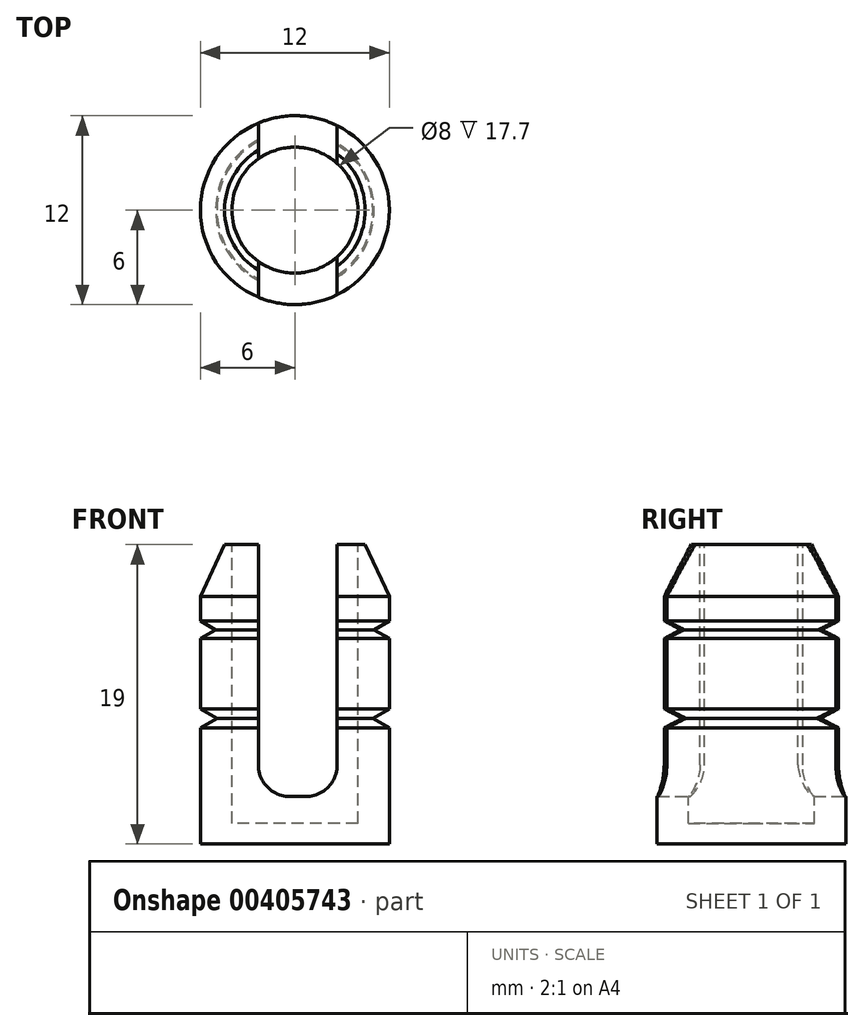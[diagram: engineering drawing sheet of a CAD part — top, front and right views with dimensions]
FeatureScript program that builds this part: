
annotation { "Feature Type Name" : "Feature", "Feature Type Description" : "" }
export const myFeature = defineFeature(function(context is Context, id is Id, definition is map)
    precondition{}
    {
        {
            var Q0;
            Q0=qCreatedBy(makeId("Top.planeOp"),FACE);
            var sketch = newSketch(context, id + "F0", { "sketchPlane" : qUnion([Q0])});
            skCircle(sketch, "E0", {"center": v(0, 0) * mm, "radius": 6 * mm});
            skSolve(sketch);
        }
        {
            var Q0;
            Q0=makeQuery(id+"F0.imprint","IMPRINT",FACE,{"disambiguationData":[TD([[makeQuery(id+"F0.imprint","IMPRINT",EDGE,{"derivedFrom":sQuery(id+"F0.wireOp",EDGE,"E0")}),1.0]])]});
            extrude(context, id + "F1", {"entities" : qUnion([Q0]), "depth" : 20 * mm});
        }
        {
            var Q0;
            Q0=makeQuery(id+"F1.opExtrude","CAP_FACE",FACE,{"disambiguationData":[OSD([sQuery(id+"F0.wireOp",EDGE,"E0")])],"isStart":false});
            var sketch = newSketch(context, id + "F2", { "sketchPlane" : qUnion([Q0])});
            skCircle(sketch, "E1", {"center": v(0, 0) * mm, "radius": 4 * mm});
            skSolve(sketch);
        }
        {
            var Q0;
            Q0 = qSketchRegion(id + "F2", true);
            extrude(context, id + "F3", {"entities" : qUnion([Q0]), "operationType" : NewBodyOperationType.REMOVE, "oppositeDirection" : true, "depth" : 18.7 * mm});
        }
        {
            var Q0;
            Q0=qCreatedBy(makeId("Front.planeOp"),FACE);
            var sketch = newSketch(context, id + "F4", { "sketchPlane" : qUnion([Q0])});
            skLineSegment(sketch, "E2", {"start": v(2.68, 16.25) * mm, "end": v(2.68, 3) * mm});
            skLineSegment(sketch, "E3", {"start": v(2.68, 3) * mm, "end": v(-2.32, 3) * mm});
            skLineSegment(sketch, "E4", {"start": v(-2.32, 3) * mm, "end": v(-2.32, 20) * mm});
            skLineSegment(sketch, "E5", {"start": v(-2.32, 20) * mm, "end": v(2.68, 20) * mm});
            skLineSegment(sketch, "E6", {"start": v(2.68, 20) * mm, "end": v(2.68, 16.25) * mm});
            skSolve(sketch);
        }
        {
            var Q0;
            Q0 = qSketchRegion(id + "F4", true);
            extrude(context, id + "F5", {"entities" : qUnion([Q0]), "operationType" : NewBodyOperationType.REMOVE, "endBound" : BoundingType.SYMMETRIC, "depth" : 25 * mm});
        }
        {
            var Q0;
            Q0=makeQuery(id+"F5.boolean.opBoolean","COPY",EDGE,{"disambiguationData":[OD(1.0)],"derivedFrom":makeQuery(id+"F5.opExtrude","SWEPT_EDGE",EDGE,{"disambiguationData":[OSD([sQuery(id+"F4.wireOp",EDGE,"E2"),sQuery(id+"F4.wireOp",EDGE,"E3")])]})});
            var Q1;
            Q1=makeQuery(id+"F5.boolean.opBoolean","COPY",EDGE,{"disambiguationData":[OD(1.0)],"derivedFrom":makeQuery(id+"F5.opExtrude","SWEPT_EDGE",EDGE,{"disambiguationData":[OSD([sQuery(id+"F4.wireOp",EDGE,"E3"),sQuery(id+"F4.wireOp",EDGE,"E4")])]})});
            var Q2;
            Q2=makeQuery(id+"F5.boolean.opBoolean","COPY",EDGE,{"disambiguationData":[OD(0.0)],"derivedFrom":makeQuery(id+"F5.opExtrude","SWEPT_EDGE",EDGE,{"disambiguationData":[OSD([sQuery(id+"F4.wireOp",EDGE,"E2"),sQuery(id+"F4.wireOp",EDGE,"E3")])]})});
            var Q3;
            Q3=makeQuery(id+"F5.boolean.opBoolean","COPY",EDGE,{"disambiguationData":[OD(0.0)],"derivedFrom":makeQuery(id+"F5.opExtrude","SWEPT_EDGE",EDGE,{"disambiguationData":[OSD([sQuery(id+"F4.wireOp",EDGE,"E3"),sQuery(id+"F4.wireOp",EDGE,"E4")])]})});
            fillet(context, id + "F6", {"entities" : qUnion([Q0, Q1, Q2, Q3]), "radius" : 2 * mm, "tangentPropagation" : true, "allowEdgeOverflow" : false});
        }
        {
            var Q0;
            {var subQ0=sQuery(id+"F0.wireOp",EDGE,"E0");Q0=makeQuery(id+"F5.boolean.opBoolean","SPLIT",EDGE,{"disambiguationData":[TD([makeQuery(id+"F5.opExtrude","SWEPT_FACE",FACE,{"disambiguationData":[OSD([sQuery(id+"F4.wireOp",EDGE,"E2"),sQuery(id+"F4.wireOp",EDGE,"E6")])]})])],"derivedFrom":makeQuery(id+"F1.opExtrude","CAP_EDGE",EDGE,{"disambiguationData":[OSD([subQ0])],"isStart":false})});}
            var Q1;
            {var subQ0=sQuery(id+"F0.wireOp",EDGE,"E0");Q1=makeQuery(id+"F5.boolean.opBoolean","SPLIT",EDGE,{"disambiguationData":[TD([makeQuery(id+"F5.opExtrude","SWEPT_FACE",FACE,{"disambiguationData":[OSD([sQuery(id+"F4.wireOp",EDGE,"E4")])]})])],"derivedFrom":makeQuery(id+"F1.opExtrude","CAP_EDGE",EDGE,{"disambiguationData":[OSD([subQ0])],"isStart":false})});}
            chamfer(context, id + "F7", {"entities" : qUnion([Q0, Q1]), "chamferType" : ChamferType.OFFSET_ANGLE, "width" : 2 * mm, "oppositeDirection" : false, "angle" : 65 * degree, "tangentPropagation" : true});
        }
        {
            var Q0;
            {var subQ0=sQuery(id+"F0.wireOp",EDGE,"E0");Q0=makeQuery(id+"F7.opChamfer","BLEND_EDGE",EDGE,{"blendedFrom":[makeQuery(id+"F5.boolean.opBoolean","SPLIT",EDGE,{"disambiguationData":[TD([makeQuery(id+"F5.opExtrude","SWEPT_FACE",FACE,{"disambiguationData":[OSD([sQuery(id+"F4.wireOp",EDGE,"E4")])]})])],"derivedFrom":makeQuery(id+"F1.opExtrude","CAP_EDGE",EDGE,{"disambiguationData":[OSD([subQ0])],"isStart":false})}),makeQuery(id+"F3.boolean.opBoolean","COPY",FACE,{"derivedFrom":makeQuery(id+"F3.opExtrude","SWEPT_FACE",FACE,{"disambiguationData":[OSD([sQuery(id+"F2.wireOp",EDGE,"E1")])]})})],"blendedInto":[makeQuery(id+"F3.boolean.opBoolean","COPY",FACE,{"derivedFrom":makeQuery(id+"F3.opExtrude","SWEPT_FACE",FACE,{"disambiguationData":[OSD([sQuery(id+"F2.wireOp",EDGE,"E1")])]})})]});}
            var Q1;
            {var subQ0=sQuery(id+"F0.wireOp",EDGE,"E0");Q1=makeQuery(id+"F7.opChamfer","BLEND_EDGE",EDGE,{"blendedFrom":[makeQuery(id+"F5.boolean.opBoolean","SPLIT",EDGE,{"disambiguationData":[TD([makeQuery(id+"F5.opExtrude","SWEPT_FACE",FACE,{"disambiguationData":[OSD([sQuery(id+"F4.wireOp",EDGE,"E2"),sQuery(id+"F4.wireOp",EDGE,"E6")])]})])],"derivedFrom":makeQuery(id+"F1.opExtrude","CAP_EDGE",EDGE,{"disambiguationData":[OSD([subQ0])],"isStart":false})}),makeQuery(id+"F3.boolean.opBoolean","COPY",FACE,{"derivedFrom":makeQuery(id+"F3.opExtrude","SWEPT_FACE",FACE,{"disambiguationData":[OSD([sQuery(id+"F2.wireOp",EDGE,"E1")])]})})],"blendedInto":[makeQuery(id+"F3.boolean.opBoolean","COPY",FACE,{"derivedFrom":makeQuery(id+"F3.opExtrude","SWEPT_FACE",FACE,{"disambiguationData":[OSD([sQuery(id+"F2.wireOp",EDGE,"E1")])]})})]});}
            chamfer(context, id + "F8", {"entities" : qUnion([Q0, Q1]), "chamferType" : ChamferType.OFFSET_ANGLE, "width" : 1 * mm, "oppositeDirection" : false, "angle" : 90 * degree, "tangentPropagation" : true});
        }
        {
            var Q0;
            Q0=qCreatedBy(makeId("Right.planeOp"),FACE);
            var sketch = newSketch(context, id + "F9", { "sketchPlane" : qUnion([Q0])});
            skLineSegment(sketch, "E7", {"start": v(-6.03, 8.6) * mm, "end": v(-6.03, 7.35) * mm});
            skLineSegment(sketch, "E8", {"start": v(-6.03, 7.35) * mm, "end": v(-4.95, 7.97) * mm});
            skLineSegment(sketch, "E9", {"start": v(-4.95, 7.97) * mm, "end": v(-6.03, 8.6) * mm});
            skSolve(sketch);
        }
        {
            var Q0;
            Q0 = qSketchRegion(id + "F9", true);
            var Q1;
            Q1 = qConstructionFilter(qBodyType(qCreatedBy(id + "F0" ,EDGE), BodyType.WIRE), ConstructionObject.NO);
            sweep(context, id + "F10", {"operationType" : NewBodyOperationType.REMOVE, "profiles" : qUnion([Q0]), "path" : qUnion([Q1])});
        }
        {
            var Q0;
            Q0=qCreatedBy(makeId("Right.planeOp"),FACE);
            var sketch = newSketch(context, id + "F11", { "sketchPlane" : qUnion([Q0])});
            skLineSegment(sketch, "E10", {"start": v(-6.12, 14.23) * mm, "end": v(-6.12, 12.98) * mm});
            skLineSegment(sketch, "E11", {"start": v(-6.12, 12.98) * mm, "end": v(-5.03, 13.6) * mm});
            skLineSegment(sketch, "E12", {"start": v(-5.03, 13.6) * mm, "end": v(-6.12, 14.23) * mm});
            skSolve(sketch);
        }
        {
            var Q0;
            Q0 = qSketchRegion(id + "F11", true);
            var Q1;
            Q1=makeQuery(id+"F1.opExtrude","CAP_EDGE",EDGE,{"disambiguationData":[OSD([sQuery(id+"F0.wireOp",EDGE,"E0")])],"isStart":true});
            revolve(context, id + "F12", {"operationType" : NewBodyOperationType.REMOVE, "entities" : qUnion([Q0]), "axis" : qUnion([Q1]), "revolveType" : RevolveType.FULL, "oppositeDirection" : true});
        }
    });
